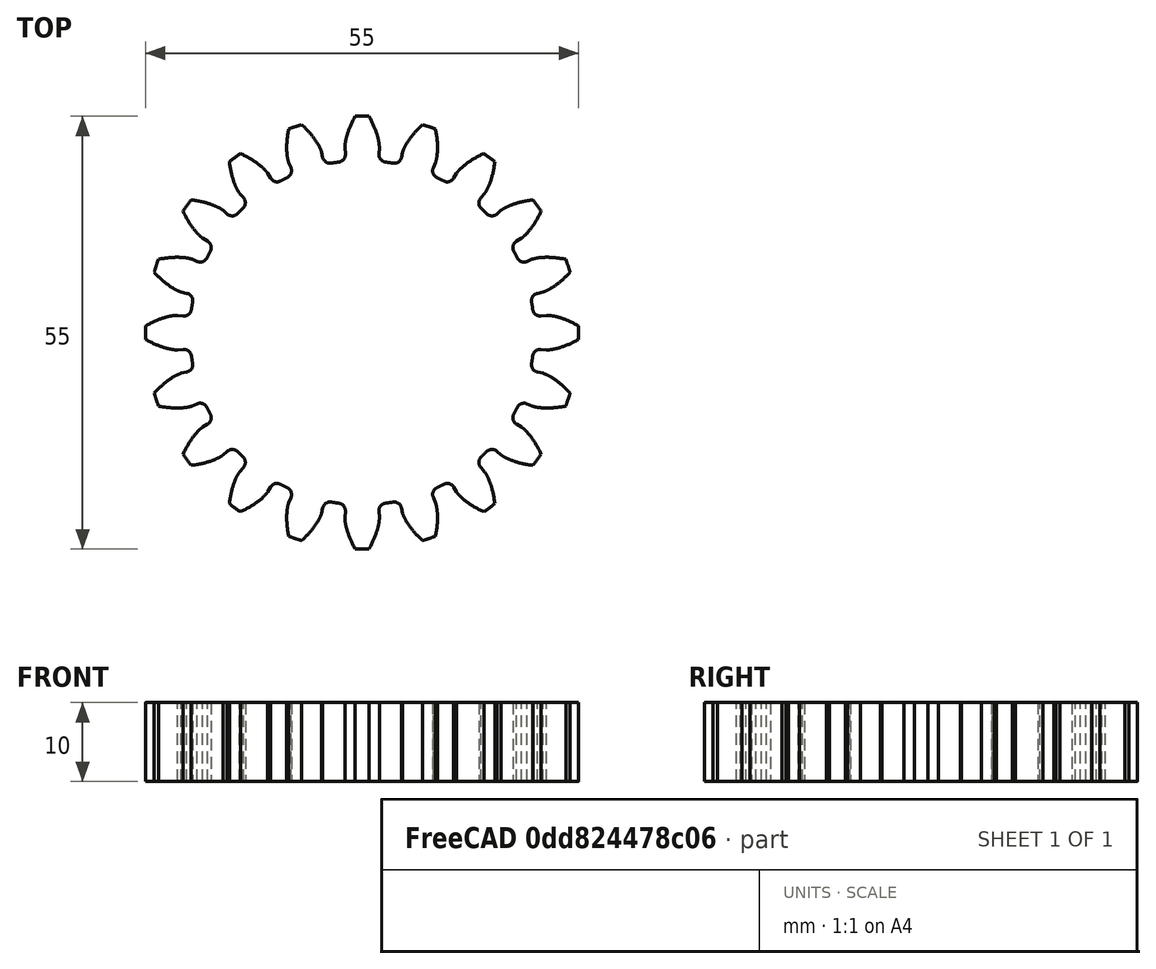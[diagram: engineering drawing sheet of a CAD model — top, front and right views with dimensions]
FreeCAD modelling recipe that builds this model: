
FCSTD DOCUMENT  (FreeCAD 1.0R39285 (Git))
Label: SteeringPinion
License: All rights reserved
LicenseURL: https://en.wikipedia.org/wiki/All_rights_reserved
objects: Part::Part2DObjectPython×1, PartDesign::Pad×1, PartDesign::Body×1
note: 5 computed .brp shape members not serialized (recipe doc carries the construction recipe); baked Part::Feature solids carry a one-line shape summary decoded from their .brp

FEATURE [Part::Part2DObjectPython] InvoluteGear  # Draft 2D object (typed FeaturePython)
  AddendumCoefficient = 1
  DedendumCoefficient = 1.25
  ExternalGear = true
  HighPrecision = true
  Modules = 2.5
  NumberOfTeeth = 20
  PressureAngle = 20
  ProfileShiftCoefficient = 0
  RootFilletCoefficient = 0.38
FEATURE [PartDesign::Pad] Pad
  Direction = (0,0,1)
  Length = 10
  Length2 = 10
  Profile = -> InvoluteGear
  ReferenceAxis = -> InvoluteGear [N_Axis]
  Refine = true
  Suppressed = false
  Type = 0
FEATURE [PartDesign::Body] Body  label="PinionBody"
  AllowCompound = false
  Group = -> [InvoluteGear,Pad]
  Origin = -> Origin
  Tip = -> Pad
